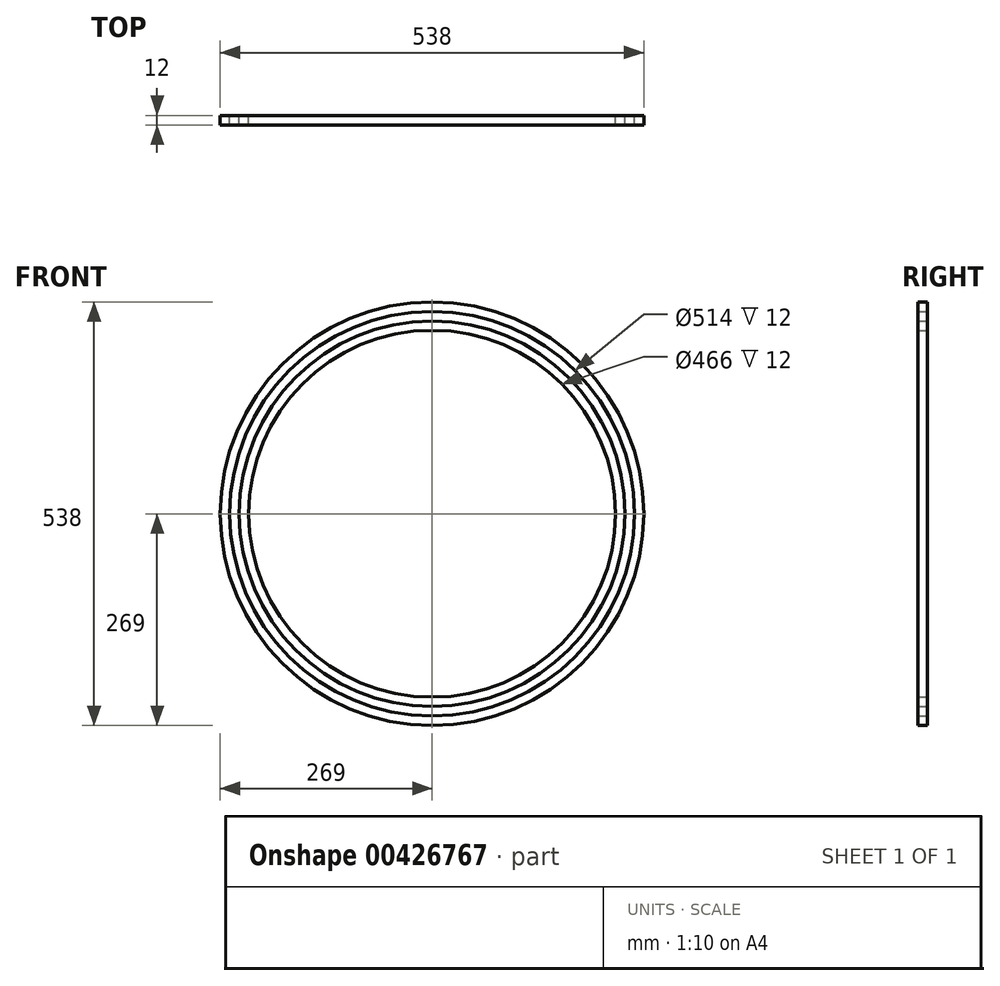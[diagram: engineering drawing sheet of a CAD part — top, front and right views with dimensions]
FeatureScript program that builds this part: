
annotation { "Feature Type Name" : "Feature", "Feature Type Description" : "" }
export const myFeature = defineFeature(function(context is Context, id is Id, definition is map)
    precondition{}
    {
        {
            var Q0;
            Q0=qCreatedBy(makeId("Front.planeOp"),FACE);
            var sketch = newSketch(context, id + "F0", { "sketchPlane" : qUnion([Q0])});
            skCircle(sketch, "E0", {"center": v(0, 0) * mm, "radius": 254 * mm, "construction": true});
            skCircle(sketch, "E1.0", {"center": v(0, 0) * mm, "radius": 248 * mm, "construction": true});
            skSolve(sketch);
        }
        {
            var Q0;
            Q0=qCreatedBy(makeId("Right.planeOp"),FACE);
            var sketch = newSketch(context, id + "F1", { "sketchPlane" : qUnion([Q0])});
            skLineSegment(sketch, "E2.0", {"start": v(0, -254) * mm, "end": v(0, 254) * mm, "construction": true});
            skLineSegment(sketch, "E3.0", {"start": v(0, -248) * mm, "end": v(0, 248) * mm, "construction": true});
            skLineSegment(sketch, "E4", {"start": v(0, 254) * mm, "end": v(19.92, 254) * mm, "construction": true});
            skLineSegment(sketch, "E5", {"start": v(0, 248) * mm, "end": v(21.66, 248) * mm, "construction": true});
            skLineSegment(sketch, "E6.bottom", {"start": v(-6, 269) * mm, "end": v(6, 269) * mm});
            skLineSegment(sketch, "E6.top", {"start": v(-6, 257) * mm, "end": v(6, 257) * mm});
            skLineSegment(sketch, "E6.left", {"start": v(-6, 269) * mm, "end": v(-6, 257) * mm});
            skLineSegment(sketch, "E6.right", {"start": v(6, 269) * mm, "end": v(6, 257) * mm});
            skLineSegment(sketch, "E7.bottom", {"start": v(-6, 257) * mm, "end": v(6, 257) * mm, "construction": true});
            skLineSegment(sketch, "E7.top", {"start": v(-6, 245) * mm, "end": v(6, 245) * mm, "construction": true});
            skLineSegment(sketch, "E7.left", {"start": v(-6, 257) * mm, "end": v(-6, 245) * mm, "construction": true});
            skLineSegment(sketch, "E7.right", {"start": v(6, 257) * mm, "end": v(6, 245) * mm, "construction": true});
            skLineSegment(sketch, "E8.bottom", {"start": v(-6, 245) * mm, "end": v(6, 245) * mm});
            skLineSegment(sketch, "E8.top", {"start": v(-6, 233) * mm, "end": v(6, 233) * mm});
            skLineSegment(sketch, "E8.left", {"start": v(-6, 245) * mm, "end": v(-6, 233) * mm});
            skLineSegment(sketch, "E8.right", {"start": v(6, 245) * mm, "end": v(6, 233) * mm});
            skSolve(sketch);
        }
        {
            var Q0;
            Q0=makeQuery(id+"F1.imprint","IMPRINT",FACE,{"disambiguationData":[TD([[makeQuery(id+"F1.imprint","IMPRINT",EDGE,{"derivedFrom":sQuery(id+"F1.wireOp",EDGE,"E6.bottom")}),-1.0]])]});
            var Q1;
            Q1=sQuery(id+"F0.wireOp",EDGE,"E0");
            revolve(context, id + "F2", {"entities" : qUnion([Q0]), "axis" : qUnion([Q1]), "revolveType" : RevolveType.FULL});
        }
        {
            var Q0;
            Q0=makeQuery(id+"F1.imprint","IMPRINT",FACE,{"disambiguationData":[TD([[makeQuery(id+"F1.imprint","IMPRINT",EDGE,{"derivedFrom":sQuery(id+"F1.wireOp",EDGE,"E8.bottom")}),-1.0]])]});
            var Q1;
            Q1=sQuery(id+"F0.wireOp",EDGE,"E1.0");
            revolve(context, id + "F3", {"entities" : qUnion([Q0]), "axis" : qUnion([Q1]), "revolveType" : RevolveType.FULL});
        }
    });
